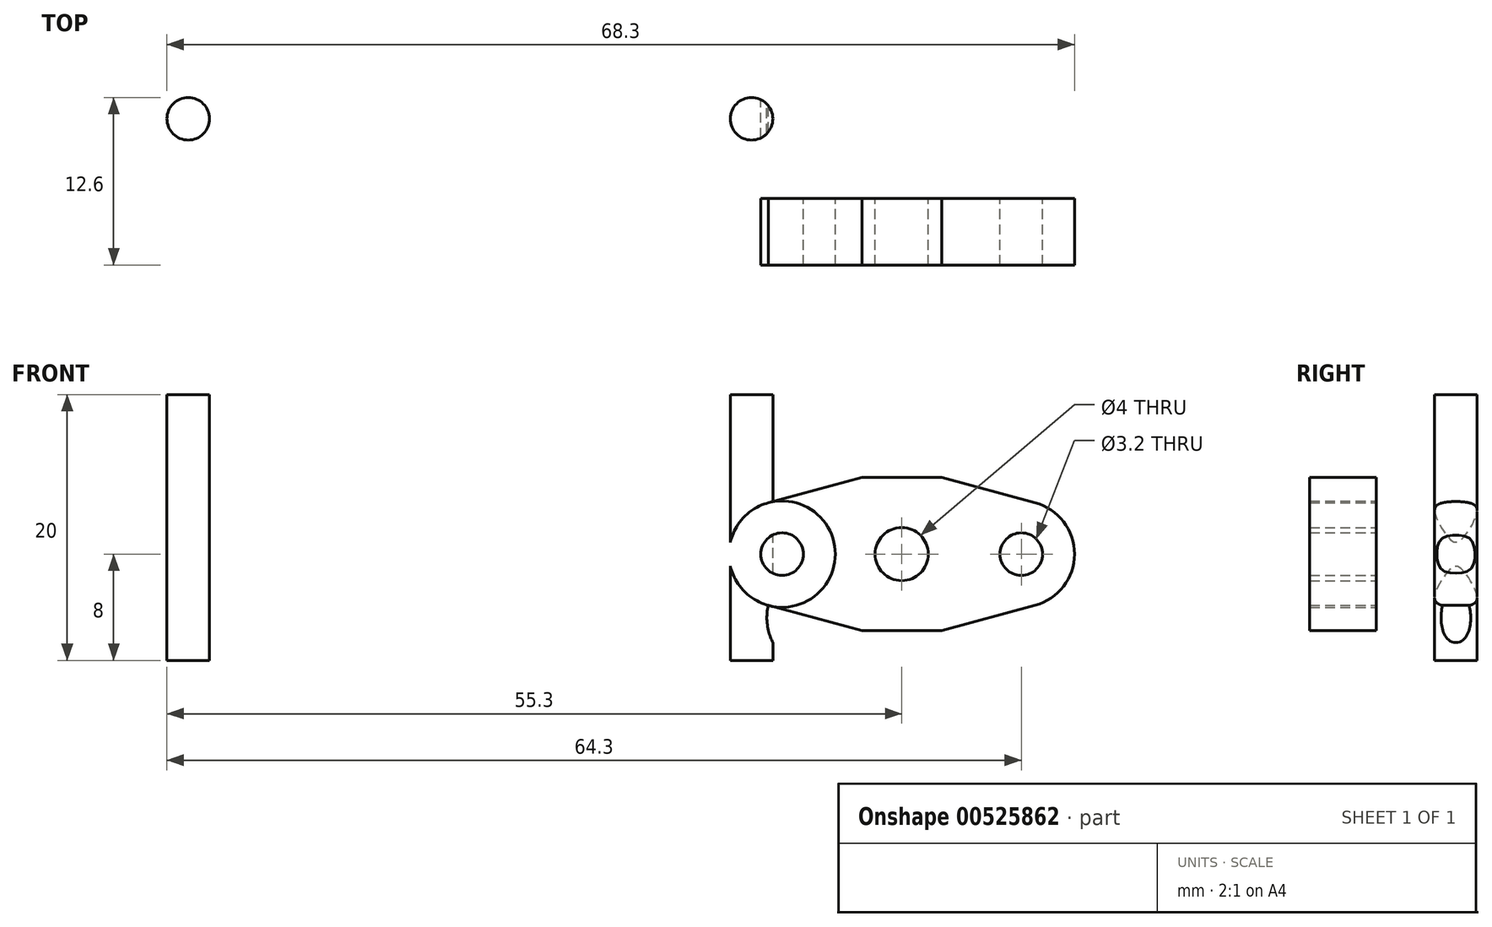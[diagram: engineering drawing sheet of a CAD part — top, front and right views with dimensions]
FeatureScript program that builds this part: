
annotation { "Feature Type Name" : "Feature", "Feature Type Description" : "" }
export const myFeature = defineFeature(function(context is Context, id is Id, definition is map)
    precondition{}
    {
        {
            var Q0;
            Q0=qCreatedBy(makeId("Top.planeOp"),FACE);
            var sketch = newSketch(context, id + "F0", { "sketchPlane" : qUnion([Q0])});
            skLineSegment(sketch, "E0.bottom", {"start": v(42.25, 6) * mm, "end": v(-42.25, 6) * mm});
            skLineSegment(sketch, "E0.top", {"start": v(42.25, -6) * mm, "end": v(-42.25, -6) * mm});
            skLineSegment(sketch, "E0.left", {"start": v(42.25, 6) * mm, "end": v(42.25, -6) * mm});
            skLineSegment(sketch, "E0.right", {"start": v(-42.25, 6) * mm, "end": v(-42.25, -6) * mm});
            skPoint(sketch, "E0.middle", {"position": v(0, 0) * mm});
            skSolve(sketch);
        }
        {
            var Q0;
            Q0 = qSketchRegion(id + "F0", true);
            extrude(context, id + "F1", {"entities" : qUnion([Q0]), "depth" : 20 * mm, "offsetDistance" : 25 * mm});
        }
        {
            var Q0;
            Q0=makeQuery(id+"F1.opExtrude","SWEPT_FACE",FACE,{"disambiguationData":[OSD([sQuery(id+"F0.wireOp",EDGE,"E0.bottom")])]});
            var sketch = newSketch(context, id + "F2", { "sketchPlane" : qUnion([Q0])});
            skLineSegment(sketch, "E1", {"start": v(0, 0) * mm, "end": v(0, 20) * mm, "construction": true});
            skLineSegment(sketch, "E2", {"start": v(17, 0) * mm, "end": v(17, 20) * mm, "construction": true});
            skPoint(sketch, "E3", {"position": v(17, 8) * mm});
            skPoint(sketch, "E4.MirrorP", {"position": v(-17, 8) * mm});
            skLineSegment(sketch, "E5.MirrorCS", {"start": v(-17, 0) * mm, "end": v(-17, 20) * mm, "construction": true});
            skCircle(sketch, "E6", {"center": v(17, 8) * mm, "radius": 6 * mm});
            skCircle(sketch, "E7", {"center": v(17, 8) * mm, "radius": 8 * mm});
            skLineSegment(sketch, "E8", {"start": v(17, 8) * mm, "end": v(25, 8) * mm, "construction": true});
            skLineSegment(sketch, "E9", {"start": v(25, 8) * mm, "end": v(25, 0) * mm});
            skLineSegment(sketch, "E10", {"start": v(25, 0) * mm, "end": v(17, 0) * mm});
            skLineSegment(sketch, "E11.MirrorCS", {"start": v(9, 8) * mm, "end": v(9, 0) * mm});
            skLineSegment(sketch, "E12.MirrorCS", {"start": v(9, 0) * mm, "end": v(17, 0) * mm});
            skLineSegment(sketch, "E13", {"start": v(23, 8) * mm, "end": v(23, 0) * mm});
            skLineSegment(sketch, "E14.MirrorCS", {"start": v(11, 8) * mm, "end": v(11, 0) * mm});
            skSolve(sketch);
        }
        {
            var Q0;
            {var subQ0=sQuery(id+"F2.wireOp",EDGE,"E6");var subQ1=makeQuery(id+"F2.imprint","INTERSECT",VERTEX,{"derivedFrom":[subQ0,sQuery(id+"F2.wireOp",EDGE,"E13")]});Q0=makeQuery(id+"F2.imprint","IMPRINT",FACE,{"disambiguationData":[TD([[makeQuery(id+"F2.imprint","IMPRINT",EDGE,{"disambiguationData":[TD([[subQ1,-1.0]])],"derivedFrom":subQ0}),1.0]])]});}
            var Q1;
            {var subQ0=sQuery(id+"F2.wireOp",EDGE,"E13");var subQ1=sQuery(id+"F2.wireOp",EDGE,"E6");var subQ2=makeQuery(id+"F2.imprint","INTERSECT",VERTEX,{"derivedFrom":[subQ1,subQ0]});Q1=makeQuery(id+"F2.imprint","IMPRINT",FACE,{"disambiguationData":[TD([[makeQuery(id+"F2.imprint","IMPRINT",EDGE,{"disambiguationData":[TD([[subQ2,1.0]])],"derivedFrom":subQ1}),-1.0]])]});}
            var Q2;
            {var subQ0=sQuery(id+"F2.wireOp",EDGE,"E10");var subQ3=sQuery(id+"F2.wireOp",EDGE,"E13");var subQ5=makeQuery(id+"F2.imprint","INTERSECT",VERTEX,{"derivedFrom":[subQ0,subQ3]});Q2=makeQuery(id+"F2.imprint","IMPRINT",FACE,{"disambiguationData":[TD([[makeQuery(id+"F2.imprint","IMPRINT",EDGE,{"disambiguationData":[TD([[subQ5,1.0]])],"derivedFrom":subQ3}),-1.0]])]});}
            var Q3;
            {var subQ0=sQuery(id+"F2.wireOp",EDGE,"E9");Q3=makeQuery(id+"F2.imprint","IMPRINT",FACE,{"disambiguationData":[TD([[makeQuery(id+"F2.imprint","IMPRINT",EDGE,{"derivedFrom":subQ0}),-1.0]])]});}
            var Q4;
            {var subQ0=sQuery(id+"F2.wireOp",EDGE,"E12.MirrorCS");var subQ3=sQuery(id+"F2.wireOp",EDGE,"E14.MirrorCS");var subQ5=makeQuery(id+"F2.imprint","INTERSECT",VERTEX,{"derivedFrom":[subQ0,subQ3]});Q4=makeQuery(id+"F2.imprint","IMPRINT",FACE,{"disambiguationData":[TD([[makeQuery(id+"F2.imprint","IMPRINT",EDGE,{"disambiguationData":[TD([[subQ5,1.0]])],"derivedFrom":subQ3}),1.0]])]});}
            var Q5;
            {var subQ0=sQuery(id+"F2.wireOp",EDGE,"E11.MirrorCS");Q5=makeQuery(id+"F2.imprint","IMPRINT",FACE,{"disambiguationData":[TD([[makeQuery(id+"F2.imprint","IMPRINT",EDGE,{"derivedFrom":subQ0}),1.0]])]});}
            var Q6;
            {var subQ2=sQuery(id+"F2.wireOp",EDGE,"E13");var subQ7=sQuery(id+"F2.wireOp",EDGE,"E6");var subQ8=makeQuery(id+"F2.imprint","INTERSECT",VERTEX,{"derivedFrom":[subQ7,subQ2]});Q6=makeQuery(id+"F2.imprint","IMPRINT",FACE,{"disambiguationData":[TD([[makeQuery(id+"F2.imprint","IMPRINT",EDGE,{"disambiguationData":[TD([[subQ8,-1.0]])],"derivedFrom":subQ7}),-1.0]])]});}
            extrude(context, id + "F3", {"entities" : qUnion([Q0, Q1, Q2, Q3, Q4, Q5, Q6]), "operationType" : NewBodyOperationType.REMOVE, "oppositeDirection" : true, "depth" : 3 * mm, "offsetDistance" : 25 * mm});
        }
        {
            var Q0;
            {var subQ0=sQuery(id+"F2.wireOp",EDGE,"E13");var subQ1=sQuery(id+"F2.wireOp",EDGE,"E6");var subQ2=makeQuery(id+"F2.imprint","INTERSECT",VERTEX,{"derivedFrom":[subQ1,subQ0]});Q0=makeQuery(id+"F2.imprint","IMPRINT",FACE,{"disambiguationData":[TD([[makeQuery(id+"F2.imprint","IMPRINT",EDGE,{"disambiguationData":[TD([[subQ2,1.0]])],"derivedFrom":subQ1}),-1.0]])]});}
            var Q1;
            {var subQ0=sQuery(id+"F2.wireOp",EDGE,"E10");var subQ3=sQuery(id+"F2.wireOp",EDGE,"E13");var subQ5=makeQuery(id+"F2.imprint","INTERSECT",VERTEX,{"derivedFrom":[subQ0,subQ3]});Q1=makeQuery(id+"F2.imprint","IMPRINT",FACE,{"disambiguationData":[TD([[makeQuery(id+"F2.imprint","IMPRINT",EDGE,{"disambiguationData":[TD([[subQ5,1.0]])],"derivedFrom":subQ3}),-1.0]])]});}
            var Q2;
            {var subQ0=sQuery(id+"F2.wireOp",EDGE,"E12.MirrorCS");var subQ3=sQuery(id+"F2.wireOp",EDGE,"E14.MirrorCS");var subQ5=makeQuery(id+"F2.imprint","INTERSECT",VERTEX,{"derivedFrom":[subQ0,subQ3]});Q2=makeQuery(id+"F2.imprint","IMPRINT",FACE,{"disambiguationData":[TD([[makeQuery(id+"F2.imprint","IMPRINT",EDGE,{"disambiguationData":[TD([[subQ5,1.0]])],"derivedFrom":subQ3}),1.0]])]});}
            var Q3;
            {var subQ0=sQuery(id+"F2.wireOp",EDGE,"E6");var subQ1=makeQuery(id+"F2.imprint","INTERSECT",VERTEX,{"derivedFrom":[subQ0,sQuery(id+"F2.wireOp",EDGE,"E13")]});Q3=makeQuery(id+"F2.imprint","IMPRINT",FACE,{"disambiguationData":[TD([[makeQuery(id+"F2.imprint","IMPRINT",EDGE,{"disambiguationData":[TD([[subQ1,-1.0]])],"derivedFrom":subQ0}),1.0]])]});}
            extrude(context, id + "F4", {"entities" : qUnion([Q0, Q1, Q2, Q3]), "operationType" : NewBodyOperationType.REMOVE, "oppositeDirection" : true, "depth" : 25 * mm, "offsetDistance" : 25 * mm});
        }
        {
            var Q0;
            Q0=makeQuery(id+"F1.opExtrude","SWEPT_FACE",FACE,{"disambiguationData":[OSD([sQuery(id+"F0.wireOp",EDGE,"E0.top")])]});
            var sketch = newSketch(context, id + "F5", { "sketchPlane" : qUnion([Q0])});
            skLineSegment(sketch, "E15.0", {"start": v(17, 0) * mm, "end": v(17, 20) * mm, "construction": true});
            skPoint(sketch, "E15.1", {"position": v(17, 8) * mm});
            skCircle(sketch, "E16", {"center": v(17, 8) * mm, "radius": 2 * mm});
            skLineSegment(sketch, "E17.bottom", {"start": v(14, 13.77) * mm, "end": v(20, 13.77) * mm});
            skLineSegment(sketch, "E17.top", {"start": v(14, 2.23) * mm, "end": v(20, 2.23) * mm});
            skLineSegment(sketch, "E17.left", {"start": v(14, 13.77) * mm, "end": v(14, 2.23) * mm});
            skLineSegment(sketch, "E17.right", {"start": v(20, 13.77) * mm, "end": v(20, 2.23) * mm});
            skLineSegment(sketch, "E18", {"start": v(17, 8) * mm, "end": v(26, 8) * mm, "construction": true});
            skCircle(sketch, "E19", {"center": v(26, 8) * mm, "radius": 1.6 * mm});
            skCircle(sketch, "E20", {"center": v(26, 8) * mm, "radius": 4 * mm});
            skLineSegment(sketch, "E21", {"start": v(20, 2.23) * mm, "end": v(27.05, 4.14) * mm});
            skLineSegment(sketch, "E22.MirrorCS", {"start": v(20, 13.77) * mm, "end": v(27.05, 11.86) * mm});
            skLineSegment(sketch, "E23.MirrorCS", {"start": v(14, 2.23) * mm, "end": v(6.95, 4.14) * mm});
            skLineSegment(sketch, "E24.MirrorCS", {"start": v(14, 13.77) * mm, "end": v(6.95, 11.86) * mm});
            skCircle(sketch, "E25.MirrorC", {"center": v(8, 8) * mm, "radius": 4 * mm});
            skCircle(sketch, "E26.MirrorC", {"center": v(8, 8) * mm, "radius": 1.6 * mm});
            skLineSegment(sketch, "E27.0", {"start": v(42.25, 0) * mm, "end": v(-9, 0) * mm});
            skLineSegment(sketch, "E28", {"start": v(20, 2.23) * mm, "end": v(20, 0) * mm});
            skLineSegment(sketch, "E29.MirrorCS", {"start": v(14, 2.23) * mm, "end": v(14, 0) * mm});
            skSolve(sketch);
        }
        {
            var Q0;
            Q0=makeQuery(id+"F5.imprint","IMPRINT",FACE,{"disambiguationData":[TD([[makeQuery(id+"F5.imprint","IMPRINT",EDGE,{"derivedFrom":sQuery(id+"F5.wireOp",EDGE,"E26.MirrorC")}),1.0]])]});
            var Q1;
            Q1=makeQuery(id+"F5.imprint","IMPRINT",FACE,{"disambiguationData":[TD([[makeQuery(id+"F5.imprint","IMPRINT",EDGE,{"derivedFrom":sQuery(id+"F5.wireOp",EDGE,"E17.left")}),-1.0]])]});
            var Q2;
            Q2=makeQuery(id+"F5.imprint","IMPRINT",FACE,{"disambiguationData":[TD([[makeQuery(id+"F5.imprint","IMPRINT",EDGE,{"derivedFrom":sQuery(id+"F5.wireOp",EDGE,"E16")}),-1.0]])]});
            var Q3;
            Q3=makeQuery(id+"F5.imprint","IMPRINT",FACE,{"disambiguationData":[TD([[makeQuery(id+"F5.imprint","IMPRINT",EDGE,{"derivedFrom":sQuery(id+"F5.wireOp",EDGE,"E17.right")}),1.0]])]});
            var Q4;
            Q4=makeQuery(id+"F5.imprint","IMPRINT",FACE,{"disambiguationData":[TD([[makeQuery(id+"F5.imprint","IMPRINT",EDGE,{"derivedFrom":sQuery(id+"F5.wireOp",EDGE,"E19")}),-1.0]])]});
            extrude(context, id + "F6", {"entities" : qUnion([Q0, Q1, Q2, Q3, Q4]), "operationType" : NewBodyOperationType.ADD, "depth" : 5 * mm, "offsetDistance" : 25 * mm});
        }
        {
            var Q0;
            Q0=makeQuery(id+"F5.imprint","IMPRINT",FACE,{"disambiguationData":[TD([[makeQuery(id+"F5.imprint","IMPRINT",EDGE,{"derivedFrom":sQuery(id+"F5.wireOp",EDGE,"E26.MirrorC")}),-1.0]])]});
            var Q1;
            Q1=makeQuery(id+"F5.imprint","IMPRINT",FACE,{"disambiguationData":[TD([[makeQuery(id+"F5.imprint","IMPRINT",EDGE,{"derivedFrom":sQuery(id+"F5.wireOp",EDGE,"E16")}),1.0]])]});
            var Q2;
            Q2=makeQuery(id+"F5.imprint","IMPRINT",FACE,{"disambiguationData":[TD([[makeQuery(id+"F5.imprint","IMPRINT",EDGE,{"derivedFrom":sQuery(id+"F5.wireOp",EDGE,"E19")}),1.0]])]});
            extrude(context, id + "F7", {"entities" : qUnion([Q0, Q1, Q2]), "operationType" : NewBodyOperationType.REMOVE, "oppositeDirection" : true, "depth" : 25 * mm, "offsetDistance" : 25 * mm});
        }
        {
            var Q0;
            {var subQ4=sQuery(id+"F2.wireOp",EDGE,"E9");Q0=makeQuery(id+"F2.imprint","IMPRINT",FACE,{"disambiguationData":[TD([[makeQuery(id+"F2.imprint","IMPRINT",EDGE,{"derivedFrom":subQ4}),1.0]])]});}
            var sketch = newSketch(context, id + "F8", { "sketchPlane" : qUnion([Q0])});
            skLineSegment(sketch, "E30.0", {"start": v(-14, 13.77) * mm, "end": v(-6.95, 11.86) * mm});
            skCircle(sketch, "E30.1", {"center": v(-8, 8) * mm, "radius": 4 * mm});
            skCircle(sketch, "E30.2", {"center": v(-8, 8) * mm, "radius": 1.6 * mm});
            skLineSegment(sketch, "E30.3", {"start": v(-14, 2.23) * mm, "end": v(-6.95, 4.14) * mm});
            skLineSegment(sketch, "E30.4", {"start": v(-14, 2.23) * mm, "end": v(-20, 2.23) * mm});
            skLineSegment(sketch, "E30.5", {"start": v(-14, 13.77) * mm, "end": v(-20, 13.77) * mm});
            skLineSegment(sketch, "E30.6", {"start": v(-20, 13.77) * mm, "end": v(-27.05, 11.86) * mm});
            skCircle(sketch, "E30.7", {"center": v(-26, 8) * mm, "radius": 4 * mm});
            skCircle(sketch, "E30.8", {"center": v(-17, 8) * mm, "radius": 2 * mm});
            skLineSegment(sketch, "E30.9", {"start": v(-20, 2.23) * mm, "end": v(-27.05, 4.14) * mm});
            skCircle(sketch, "E30.10", {"center": v(-26, 8) * mm, "radius": 1.6 * mm});
            skLineSegment(sketch, "E31.0", {"start": v(-17, 8) * mm, "end": v(-26, 8) * mm, "construction": true});
            skLineSegment(sketch, "E32", {"start": v(-30, 8) * mm, "end": v(-30, 20.01) * mm});
            skLineSegment(sketch, "E33", {"start": v(-4, 8) * mm, "end": v(-4, 20.01) * mm});
            skLineSegment(sketch, "E34", {"start": v(-4, 20.01) * mm, "end": v(-30, 20.01) * mm});
            skLineSegment(sketch, "E35", {"start": v(-30, 8) * mm, "end": v(-30, 0) * mm});
            skLineSegment(sketch, "E36", {"start": v(-4, 8) * mm, "end": v(-4, 0) * mm});
            skLineSegment(sketch, "E37", {"start": v(-4, 0) * mm, "end": v(-30, 0) * mm});
            skArc(sketch, "E38", {"start": v(-8.4, 0) * mm, "mid": v(-7.08, 1.86) * mm, "end": v(-6.95, 4.14) * mm});
            skSolve(sketch);
        }
        {
            var Q0;
            {var subQ2=sQuery(id+"F8.wireOp",EDGE,"E30.0");Q0=makeQuery(id+"F8.imprint","IMPRINT",FACE,{"disambiguationData":[TD([[makeQuery(id+"F8.imprint","IMPRINT",EDGE,{"derivedFrom":subQ2}),-1.0]])]});}
            var Q1;
            Q1=makeQuery(id+"F8.imprint","IMPRINT",FACE,{"disambiguationData":[TD([[makeQuery(id+"F8.imprint","IMPRINT",EDGE,{"derivedFrom":sQuery(id+"F8.wireOp",EDGE,"E30.2")}),-1.0]])]});
            var Q2;
            Q2=makeQuery(id+"F8.imprint","IMPRINT",FACE,{"disambiguationData":[TD([[makeQuery(id+"F8.imprint","IMPRINT",EDGE,{"derivedFrom":sQuery(id+"F8.wireOp",EDGE,"E30.10")}),1.0]])]});
            extrude(context, id + "F9", {"entities" : qUnion([Q0, Q1, Q2]), "operationType" : NewBodyOperationType.REMOVE, "oppositeDirection" : true, "depth" : 10 * mm, "offsetDistance" : 25 * mm});
        }
        {
            var Q0;
            Q0=makeQuery(id+"F1.opExtrude","CAP_FACE",FACE,{"disambiguationData":[OSD([sQuery(id+"F0.wireOp",EDGE,"E0.bottom"),sQuery(id+"F0.wireOp",EDGE,"E0.top"),sQuery(id+"F0.wireOp",EDGE,"E0.left"),sQuery(id+"F0.wireOp",EDGE,"E0.right")])],"isStart":false});
            var sketch = newSketch(context, id + "F10", { "sketchPlane" : qUnion([Q0])});
            skPoint(sketch, "E39.0", {"position": v(0, 6) * mm});
            skPoint(sketch, "E40.0", {"position": v(0, -6) * mm});
            skLineSegment(sketch, "E41", {"start": v(0, 6) * mm, "end": v(0, -6) * mm, "construction": true});
            skPoint(sketch, "E42", {"position": v(0, 0) * mm});
            skLineSegment(sketch, "E43", {"start": v(0, 0) * mm, "end": v(-21.2, 0) * mm, "construction": true});
            skLineSegment(sketch, "E44", {"start": v(-21.2, 0) * mm, "end": v(-21.2, -2.58) * mm, "construction": true});
            skCircle(sketch, "E45", {"center": v(-5.7, 0) * mm, "radius": 1.6 * mm});
            skCircle(sketch, "E46.MirrorC", {"center": v(-36.7, 0) * mm, "radius": 1.6 * mm});
            skCircle(sketch, "E47.MirrorC", {"center": v(5.7, 0) * mm, "radius": 1.6 * mm});
            skCircle(sketch, "E48.MirrorC", {"center": v(36.7, 0) * mm, "radius": 1.6 * mm});
            skSolve(sketch);
        }
        {
            var Q0;
            Q0=makeQuery(id+"F10.imprint","IMPRINT",FACE,{"disambiguationData":[TD([[makeQuery(id+"F10.imprint","IMPRINT",EDGE,{"derivedFrom":sQuery(id+"F10.wireOp",EDGE,"E46.MirrorC")}),-1.0]])]});
            var Q1;
            Q1=makeQuery(id+"F10.imprint","IMPRINT",FACE,{"disambiguationData":[TD([[makeQuery(id+"F10.imprint","IMPRINT",EDGE,{"derivedFrom":sQuery(id+"F10.wireOp",EDGE,"E45")}),1.0]])]});
            var Q2;
            Q2=makeQuery(id+"F10.imprint","IMPRINT",FACE,{"disambiguationData":[TD([[makeQuery(id+"F10.imprint","IMPRINT",EDGE,{"derivedFrom":sQuery(id+"F10.wireOp",EDGE,"E47.MirrorC")}),-1.0]])]});
            var Q3;
            Q3=makeQuery(id+"F10.imprint","IMPRINT",FACE,{"disambiguationData":[TD([[makeQuery(id+"F10.imprint","IMPRINT",EDGE,{"derivedFrom":sQuery(id+"F10.wireOp",EDGE,"E48.MirrorC")}),1.0]])]});
            extrude(context, id + "F11", {"entities" : qUnion([Q0, Q1, Q2, Q3]), "operationType" : NewBodyOperationType.REMOVE, "oppositeDirection" : true, "depth" : 25 * mm, "offsetDistance" : 25 * mm});
        }
        {
            var Q0;
            {var subQ4=sQuery(id+"F2.wireOp",EDGE,"E9");Q0=makeQuery(id+"F2.imprint","IMPRINT",FACE,{"disambiguationData":[TD([[makeQuery(id+"F2.imprint","IMPRINT",EDGE,{"derivedFrom":subQ4}),1.0]])]});}
            var sketch = newSketch(context, id + "F12", { "sketchPlane" : qUnion([Q0])});
            skCircle(sketch, "E49.0", {"center": v(-8, 8) * mm, "radius": 1.6 * mm});
            skCircle(sketch, "E49.1", {"center": v(-26, 8) * mm, "radius": 1.6 * mm});
            skCircle(sketch, "E50.cCircle", {"center": v(-8, 8) * mm, "radius": 2.8 * mm, "construction": true});
            skLineSegment(sketch, "E50.0", {"start": v(-9.37, 10.44) * mm, "end": v(-6.57, 10.4) * mm});
            skLineSegment(sketch, "E50.1", {"start": v(-6.57, 10.4) * mm, "end": v(-5.2, 7.96) * mm});
            skLineSegment(sketch, "E50.2", {"start": v(-5.2, 7.96) * mm, "end": v(-6.63, 5.56) * mm});
            skLineSegment(sketch, "E50.3", {"start": v(-6.63, 5.56) * mm, "end": v(-9.43, 5.6) * mm});
            skLineSegment(sketch, "E50.4", {"start": v(-9.43, 5.6) * mm, "end": v(-10.8, 8.04) * mm});
            skLineSegment(sketch, "E50.5", {"start": v(-10.8, 8.04) * mm, "end": v(-9.37, 10.44) * mm});
            skLineSegment(sketch, "E51.0", {"start": v(-17, 0) * mm, "end": v(-17, 20) * mm, "construction": true});
            skLineSegment(sketch, "E52.MirrorCS", {"start": v(-27.37, 5.56) * mm, "end": v(-24.57, 5.6) * mm});
            skLineSegment(sketch, "E53.MirrorCS", {"start": v(-24.57, 5.6) * mm, "end": v(-23.2, 8.04) * mm});
            skLineSegment(sketch, "E54.MirrorCS", {"start": v(-23.2, 8.04) * mm, "end": v(-24.63, 10.44) * mm});
            skLineSegment(sketch, "E55.MirrorCS", {"start": v(-28.8, 7.96) * mm, "end": v(-27.37, 5.56) * mm});
            skLineSegment(sketch, "E56.MirrorCS", {"start": v(-24.63, 10.44) * mm, "end": v(-27.43, 10.4) * mm});
            skLineSegment(sketch, "E57.MirrorCS", {"start": v(-27.43, 10.4) * mm, "end": v(-28.8, 7.96) * mm});
            skCircle(sketch, "E58.MirrorC", {"center": v(-26, 8) * mm, "radius": 2.8 * mm, "construction": true});
            skSolve(sketch);
        }
        {
            var Q0;
            Q0=makeQuery(id+"F12.imprint","IMPRINT",FACE,{"disambiguationData":[TD([[makeQuery(id+"F12.imprint","IMPRINT",EDGE,{"derivedFrom":sQuery(id+"F12.wireOp",EDGE,"E49.0")}),-1.0]])]});
            var Q1;
            Q1=makeQuery(id+"F12.imprint","IMPRINT",FACE,{"disambiguationData":[TD([[makeQuery(id+"F12.imprint","IMPRINT",EDGE,{"derivedFrom":sQuery(id+"F12.wireOp",EDGE,"E52.MirrorCS")}),1.0]])]});
            extrude(context, id + "F13", {"entities" : qUnion([Q0, Q1]), "operationType" : NewBodyOperationType.REMOVE, "oppositeDirection" : true, "depth" : 12 * mm, "offsetDistance" : 25 * mm});
        }
        {
            var Q0;
            {var subQ3=sQuery(id+"F8.wireOp",EDGE,"E30.3");Q0=makeQuery(id+"F8.imprint","IMPRINT",FACE,{"disambiguationData":[TD([[makeQuery(id+"F8.imprint","IMPRINT",EDGE,{"derivedFrom":subQ3}),-1.0]])]});}
            extrude(context, id + "F14", {"entities" : qUnion([Q0]), "operationType" : NewBodyOperationType.REMOVE, "oppositeDirection" : true, "depth" : 10 * mm, "offsetDistance" : 25 * mm});
        }
    });
